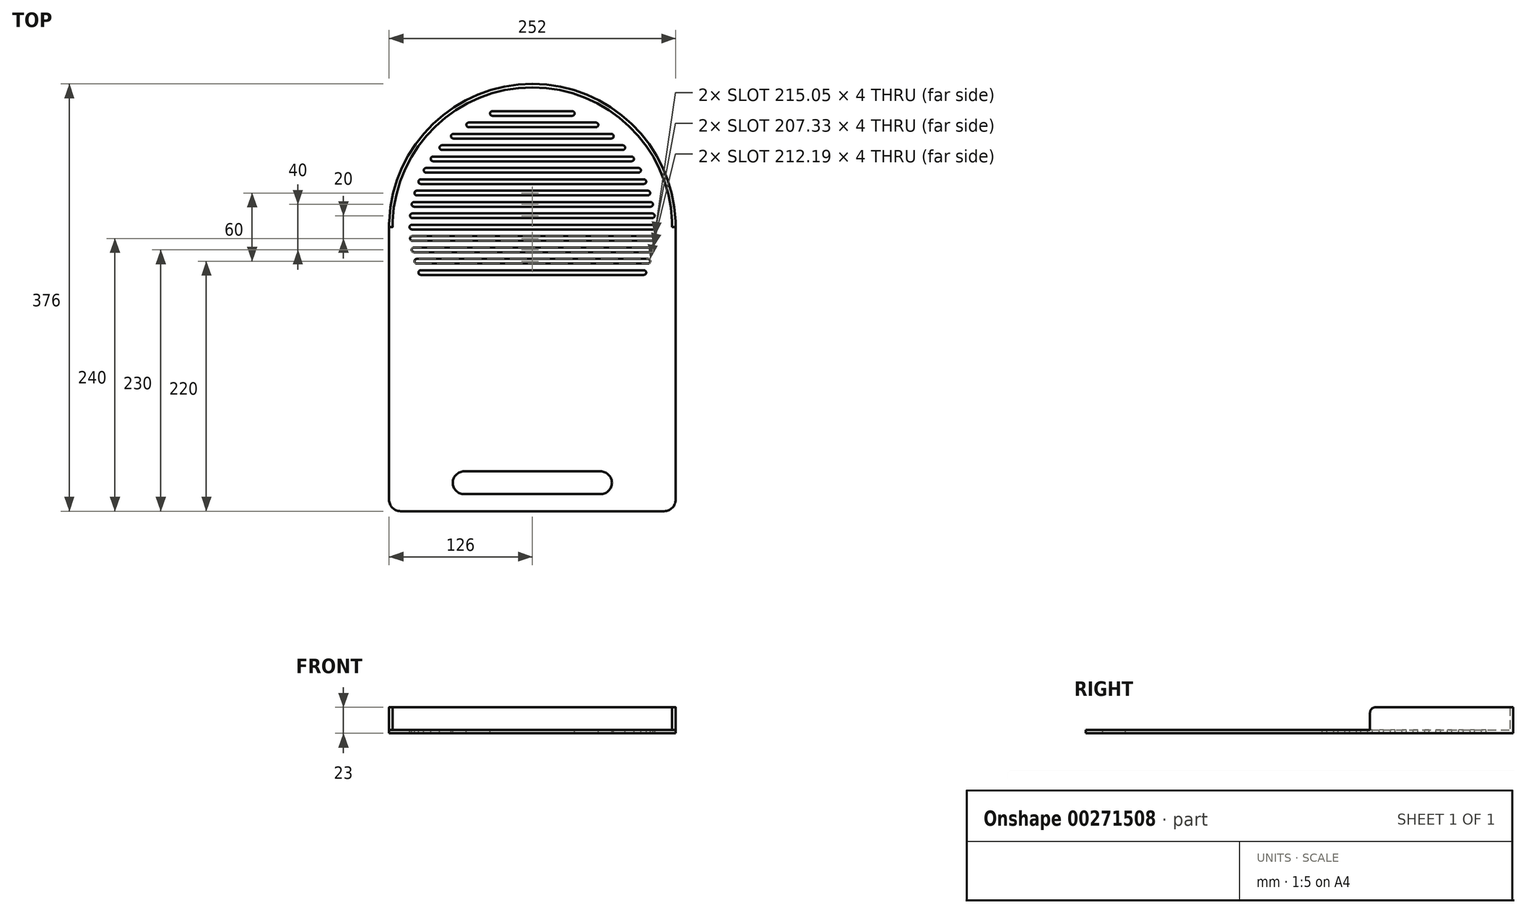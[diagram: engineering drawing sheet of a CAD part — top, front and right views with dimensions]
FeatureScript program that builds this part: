
annotation { "Feature Type Name" : "Feature", "Feature Type Description" : "" }
export const myFeature = defineFeature(function(context is Context, id is Id, definition is map)
    precondition{}
    {
        {
            var Q0;
            Q0=qCreatedBy(makeId("Top.planeOp"),FACE);
            var sketch = newSketch(context, id + "F0", { "sketchPlane" : qUnion([Q0])});
            skArc(sketch, "E0", {"start": v(126, 0) * mm, "mid": v(0, 126) * mm, "end": v(-126, 0) * mm});
            skLineSegment(sketch, "E1.top", {"start": v(-116, -250) * mm, "end": v(116, -250) * mm});
            skLineSegment(sketch, "E1.left", {"start": v(-126, 0) * mm, "end": v(-126, -240) * mm});
            skLineSegment(sketch, "E1.right", {"start": v(126, 0) * mm, "end": v(126, -240) * mm});
            skPoint(sketch, "E2.visualSharp", {"position": v(-126, -250) * mm});
            skArc(sketch, "E2.filletArc", {"start": v(-126, -240) * mm, "mid": v(-123.07, -247.07) * mm, "end": v(-116, -250) * mm});
            skPoint(sketch, "E3.visualSharp", {"position": v(126, -250) * mm});
            skArc(sketch, "E3.filletArc", {"start": v(116, -250) * mm, "mid": v(123.07, -247.07) * mm, "end": v(126, -240) * mm});
            skArc(sketch, "E4.0", {"start": v(123, 0) * mm, "mid": v(0, 123) * mm, "end": v(-123, 0) * mm});
            skLineSegment(sketch, "E5", {"start": v(-123, 0) * mm, "end": v(-126, 0) * mm});
            skLineSegment(sketch, "E6", {"start": v(123, 0) * mm, "end": v(126, 0) * mm});
            skLineSegment(sketch, "E7", {"start": v(-106, 0) * mm, "end": v(106, 0) * mm});
            skLineSegment(sketch, "E8", {"start": v(-105.53, 10) * mm, "end": v(105.53, 10) * mm});
            skLineSegment(sketch, "E9", {"start": v(-104.1, 20) * mm, "end": v(104.1, 20) * mm});
            skLineSegment(sketch, "E10", {"start": v(-101.67, 30) * mm, "end": v(101.67, 30) * mm});
            skLineSegment(sketch, "E11", {"start": v(-98.16, 40) * mm, "end": v(98.16, 40) * mm, "construction": true});
            skArc(sketch, "E12.0", {"start": v(106, 0) * mm, "mid": v(0, 106) * mm, "end": v(-106, 0) * mm, "construction": true});
            skArc(sketch, "E13.0.startCap", {"start": v(-106, -2) * mm, "mid": v(-108, 0) * mm, "end": v(-106, 2) * mm});
            skArc(sketch, "E13.0.endCap", {"start": v(106, 2) * mm, "mid": v(108, 0) * mm, "end": v(106, -2) * mm});
            skLineSegment(sketch, "E13.0.left", {"start": v(-106, 2) * mm, "end": v(106, 2) * mm});
            skLineSegment(sketch, "E13.0.right", {"start": v(-106, -2) * mm, "end": v(106, -2) * mm});
            skArc(sketch, "E14.0.startCap", {"start": v(-105.53, 8) * mm, "mid": v(-107.53, 10) * mm, "end": v(-105.53, 12) * mm});
            skArc(sketch, "E14.0.endCap", {"start": v(105.53, 12) * mm, "mid": v(107.53, 10) * mm, "end": v(105.53, 8) * mm});
            skLineSegment(sketch, "E14.0.left", {"start": v(-105.53, 12) * mm, "end": v(105.53, 12) * mm});
            skLineSegment(sketch, "E14.0.right", {"start": v(-105.53, 8) * mm, "end": v(105.53, 8) * mm});
            skArc(sketch, "E14.1.startCap", {"start": v(-104.1, 18) * mm, "mid": v(-106.1, 20) * mm, "end": v(-104.1, 22) * mm});
            skArc(sketch, "E14.1.endCap", {"start": v(104.1, 22) * mm, "mid": v(106.1, 20) * mm, "end": v(104.1, 18) * mm});
            skLineSegment(sketch, "E14.1.left", {"start": v(-104.1, 22) * mm, "end": v(104.1, 22) * mm});
            skLineSegment(sketch, "E14.1.right", {"start": v(-104.1, 18) * mm, "end": v(104.1, 18) * mm});
            skArc(sketch, "E14.2.startCap", {"start": v(-101.67, 28) * mm, "mid": v(-103.67, 30) * mm, "end": v(-101.67, 32) * mm});
            skArc(sketch, "E14.2.endCap", {"start": v(101.67, 32) * mm, "mid": v(103.67, 30) * mm, "end": v(101.67, 28) * mm});
            skLineSegment(sketch, "E14.2.left", {"start": v(-101.67, 32) * mm, "end": v(101.67, 32) * mm});
            skLineSegment(sketch, "E14.2.right", {"start": v(-101.67, 28) * mm, "end": v(101.67, 28) * mm});
            skArc(sketch, "E14.3.startCap", {"start": v(-98.16, 38) * mm, "mid": v(-100.16, 40) * mm, "end": v(-98.16, 42) * mm});
            skArc(sketch, "E14.3.endCap", {"start": v(98.16, 42) * mm, "mid": v(100.16, 40) * mm, "end": v(98.16, 38) * mm});
            skLineSegment(sketch, "E14.3.left", {"start": v(-98.16, 42) * mm, "end": v(98.16, 42) * mm});
            skLineSegment(sketch, "E14.3.right", {"start": v(-98.16, 38) * mm, "end": v(98.16, 38) * mm});
            skArc(sketch, "E15.MirrorCS", {"start": v(-105.53, -8) * mm, "mid": v(-107.53, -10) * mm, "end": v(-105.53, -12) * mm});
            skLineSegment(sketch, "E16.MirrorCS", {"start": v(-105.53, -12) * mm, "end": v(105.53, -12) * mm});
            skLineSegment(sketch, "E17.MirrorCS", {"start": v(-105.53, -8) * mm, "end": v(105.53, -8) * mm});
            skArc(sketch, "E18.MirrorCS", {"start": v(105.53, -12) * mm, "mid": v(107.53, -10) * mm, "end": v(105.53, -8) * mm});
            skArc(sketch, "E19.MirrorCS", {"start": v(98.16, -42) * mm, "mid": v(100.16, -40) * mm, "end": v(98.16, -38) * mm});
            skLineSegment(sketch, "E20.MirrorCS", {"start": v(-98.16, -42) * mm, "end": v(98.16, -42) * mm});
            skLineSegment(sketch, "E21.MirrorCS", {"start": v(-98.16, -38) * mm, "end": v(98.16, -38) * mm});
            skArc(sketch, "E22.MirrorCS", {"start": v(-98.16, -38) * mm, "mid": v(-100.16, -40) * mm, "end": v(-98.16, -42) * mm});
            skArc(sketch, "E23.MirrorCS", {"start": v(-101.67, -28) * mm, "mid": v(-103.67, -30) * mm, "end": v(-101.67, -32) * mm});
            skLineSegment(sketch, "E24.MirrorCS", {"start": v(-101.67, -32) * mm, "end": v(101.67, -32) * mm});
            skLineSegment(sketch, "E25.MirrorCS", {"start": v(-101.67, -28) * mm, "end": v(101.67, -28) * mm});
            skArc(sketch, "E26.MirrorCS", {"start": v(101.67, -32) * mm, "mid": v(103.67, -30) * mm, "end": v(101.67, -28) * mm});
            skArc(sketch, "E27.MirrorCS", {"start": v(104.1, -22) * mm, "mid": v(106.1, -20) * mm, "end": v(104.1, -18) * mm});
            skLineSegment(sketch, "E28.MirrorCS", {"start": v(-104.1, -22) * mm, "end": v(104.1, -22) * mm});
            skLineSegment(sketch, "E29.MirrorCS", {"start": v(-104.1, -18) * mm, "end": v(104.1, -18) * mm});
            skArc(sketch, "E30.MirrorCS", {"start": v(-104.1, -18) * mm, "mid": v(-106.1, -20) * mm, "end": v(-104.1, -22) * mm});
            skLineSegment(sketch, "E31", {"start": v(-60, -225) * mm, "end": v(60, -225) * mm});
            skLineSegment(sketch, "E32", {"start": v(0, -126) * mm, "end": v(0, -250) * mm, "construction": true});
            skPoint(sketch, "E33", {"position": v(0, -225) * mm});
            skArc(sketch, "E34.0.startCap", {"start": v(-60, -235) * mm, "mid": v(-70, -225) * mm, "end": v(-60, -215) * mm});
            skArc(sketch, "E34.0.endCap", {"start": v(60, -215) * mm, "mid": v(70, -225) * mm, "end": v(60, -235) * mm});
            skLineSegment(sketch, "E34.0.left", {"start": v(-60, -215) * mm, "end": v(60, -215) * mm});
            skLineSegment(sketch, "E34.0.right", {"start": v(-60, -235) * mm, "end": v(60, -235) * mm});
            skLineSegment(sketch, "E35", {"start": v(-93.47, 50) * mm, "end": v(93.47, 50) * mm});
            skLineSegment(sketch, "E36", {"start": v(-87.38, 60) * mm, "end": v(87.38, 60) * mm});
            skLineSegment(sketch, "E37", {"start": v(-79.6, 70) * mm, "end": v(79.6, 70) * mm});
            skLineSegment(sketch, "E38", {"start": v(-69.54, 80) * mm, "end": v(69.54, 80) * mm});
            skLineSegment(sketch, "E39", {"start": v(-56, 90) * mm, "end": v(56, 90) * mm});
            skLineSegment(sketch, "E40", {"start": v(-35.16, 100) * mm, "end": v(35.16, 100) * mm});
            skArc(sketch, "E41.0.startCap", {"start": v(-93.47, 48) * mm, "mid": v(-95.47, 50) * mm, "end": v(-93.47, 52) * mm});
            skArc(sketch, "E41.0.endCap", {"start": v(93.47, 52) * mm, "mid": v(95.47, 50) * mm, "end": v(93.47, 48) * mm});
            skLineSegment(sketch, "E41.0.left", {"start": v(-93.47, 52) * mm, "end": v(93.47, 52) * mm});
            skLineSegment(sketch, "E41.0.right", {"start": v(-93.47, 48) * mm, "end": v(93.47, 48) * mm});
            skArc(sketch, "E42.0.startCap", {"start": v(-79.6, 68) * mm, "mid": v(-81.6, 70) * mm, "end": v(-79.6, 72) * mm});
            skArc(sketch, "E42.0.endCap", {"start": v(79.6, 72) * mm, "mid": v(81.6, 70) * mm, "end": v(79.6, 68) * mm});
            skLineSegment(sketch, "E42.0.left", {"start": v(-79.6, 72) * mm, "end": v(79.6, 72) * mm});
            skLineSegment(sketch, "E42.0.right", {"start": v(-79.6, 68) * mm, "end": v(79.6, 68) * mm});
            skArc(sketch, "E43.0.startCap", {"start": v(-56, 88) * mm, "mid": v(-58, 90) * mm, "end": v(-56, 92) * mm});
            skArc(sketch, "E43.0.endCap", {"start": v(56, 92) * mm, "mid": v(58, 90) * mm, "end": v(56, 88) * mm});
            skLineSegment(sketch, "E43.0.left", {"start": v(-56, 92) * mm, "end": v(56, 92) * mm});
            skLineSegment(sketch, "E43.0.right", {"start": v(-56, 88) * mm, "end": v(56, 88) * mm});
            skArc(sketch, "E44.0.startCap", {"start": v(-87.38, 58) * mm, "mid": v(-89.38, 60) * mm, "end": v(-87.38, 62) * mm});
            skArc(sketch, "E44.0.endCap", {"start": v(87.38, 62) * mm, "mid": v(89.38, 60) * mm, "end": v(87.38, 58) * mm});
            skLineSegment(sketch, "E44.0.left", {"start": v(-87.38, 62) * mm, "end": v(87.38, 62) * mm});
            skLineSegment(sketch, "E44.0.right", {"start": v(-87.38, 58) * mm, "end": v(87.38, 58) * mm});
            skArc(sketch, "E45.0.startCap", {"start": v(-69.54, 78) * mm, "mid": v(-71.54, 80) * mm, "end": v(-69.54, 82) * mm});
            skArc(sketch, "E45.0.endCap", {"start": v(69.54, 82) * mm, "mid": v(71.54, 80) * mm, "end": v(69.54, 78) * mm});
            skLineSegment(sketch, "E45.0.left", {"start": v(-69.54, 82) * mm, "end": v(69.54, 82) * mm});
            skLineSegment(sketch, "E45.0.right", {"start": v(-69.54, 78) * mm, "end": v(69.54, 78) * mm});
            skArc(sketch, "E46.0.startCap", {"start": v(-35.16, 98) * mm, "mid": v(-37.16, 100) * mm, "end": v(-35.16, 102) * mm});
            skArc(sketch, "E46.0.endCap", {"start": v(35.16, 102) * mm, "mid": v(37.16, 100) * mm, "end": v(35.16, 98) * mm});
            skLineSegment(sketch, "E46.0.left", {"start": v(-35.16, 102) * mm, "end": v(35.16, 102) * mm});
            skLineSegment(sketch, "E46.0.right", {"start": v(-35.16, 98) * mm, "end": v(35.16, 98) * mm});
            skSolve(sketch);
        }
        {
            var Q0;
            Q0=makeQuery(id+"F0.imprint","IMPRINT",FACE,{"disambiguationData":[TD([[makeQuery(id+"F0.imprint","IMPRINT",EDGE,{"derivedFrom":sQuery(id+"F0.wireOp",EDGE,"E1.top")}),1.0]])]});
            var Q1;
            Q1=makeQuery(id+"F0.imprint","IMPRINT",FACE,{"disambiguationData":[TD([[makeQuery(id+"F0.imprint","IMPRINT",EDGE,{"derivedFrom":sQuery(id+"F0.wireOp",EDGE,"E0")}),1.0]])]});
            extrude(context, id + "F1", {"entities" : qUnion([Q0, Q1]), "oppositeDirection" : true, "depth" : 3 * mm});
        }
        {
            var Q0;
            Q0=makeQuery(id+"F0.imprint","IMPRINT",FACE,{"disambiguationData":[TD([[makeQuery(id+"F0.imprint","IMPRINT",EDGE,{"derivedFrom":sQuery(id+"F0.wireOp",EDGE,"E0")}),1.0]])]});
            extrude(context, id + "F2", {"entities" : qUnion([Q0]), "operationType" : NewBodyOperationType.ADD, "depth" : 20 * mm});
        }
        {
            var Q0;
            Q0=makeQuery(id+"F2.opExtrude","CAP_EDGE",EDGE,{"disambiguationData":[OSD([sQuery(id+"F0.wireOp",EDGE,"E5")])],"isStart":false});
            var Q1;
            Q1=makeQuery(id+"F2.opExtrude","CAP_EDGE",EDGE,{"disambiguationData":[OSD([sQuery(id+"F0.wireOp",EDGE,"E6")])],"isStart":false});
            fillet(context, id + "F3", {"entities" : qUnion([Q0, Q1]), "radius" : 5 * mm, "tangentPropagation" : true, "allowEdgeOverflow" : false});
        }
    });
